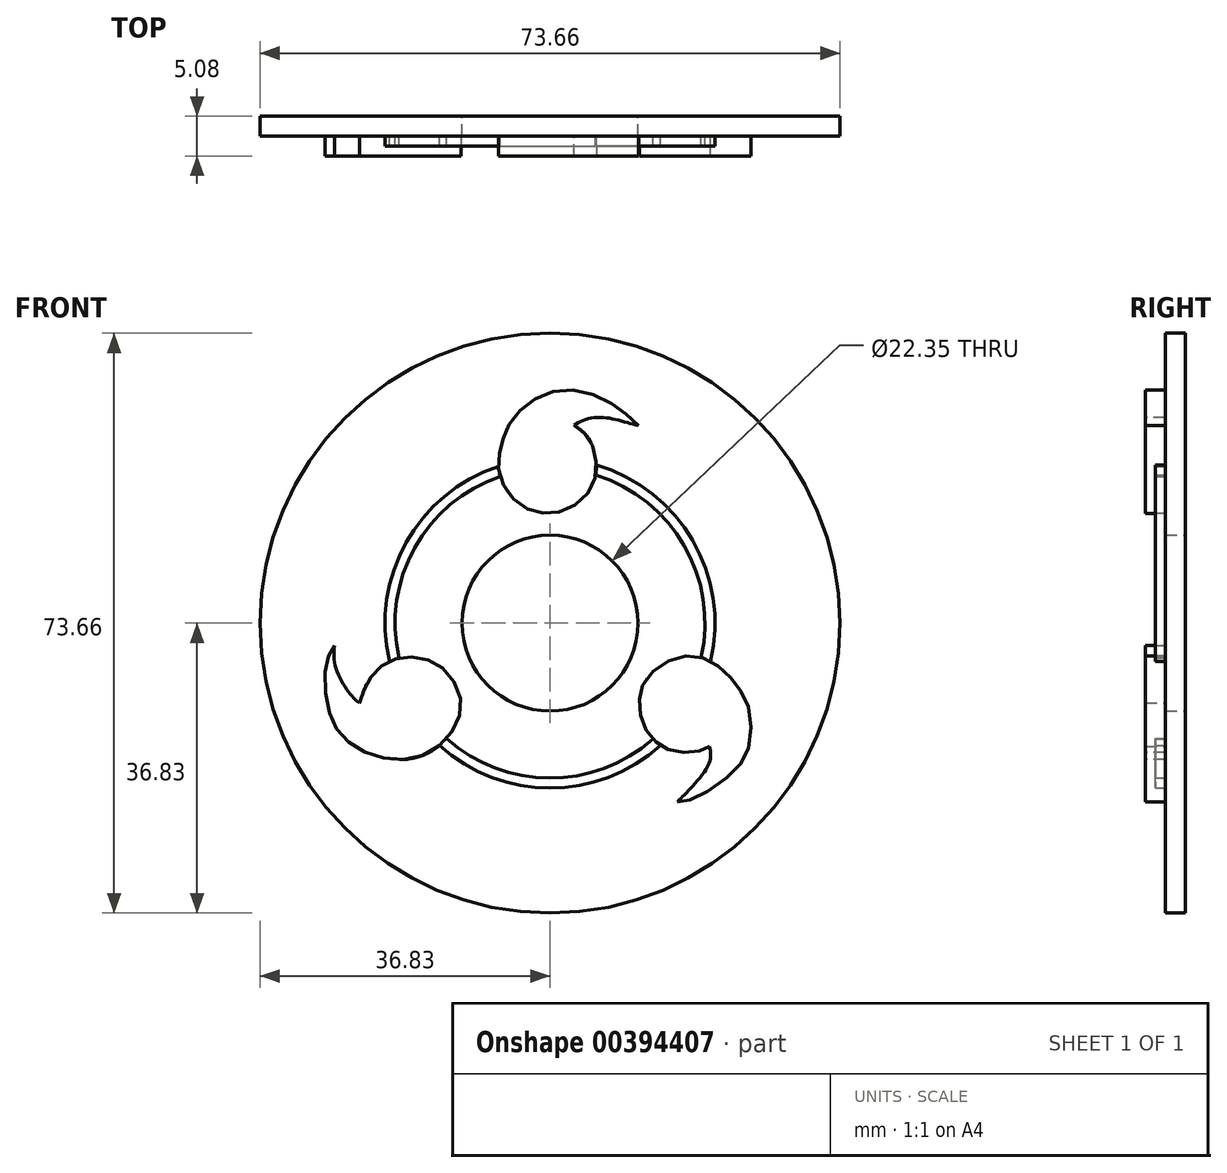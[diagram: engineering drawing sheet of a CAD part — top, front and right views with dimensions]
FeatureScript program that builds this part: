
annotation { "Feature Type Name" : "Feature", "Feature Type Description" : "" }
export const myFeature = defineFeature(function(context is Context, id is Id, definition is map)
    precondition{}
    {
        {
            var Q0;
            Q0=qCreatedBy(makeId("Front.planeOp"),FACE);
            var sketch = newSketch(context, id + "F0", { "sketchPlane" : qUnion([Q0])});
            skCircle(sketch, "E0", {"center": v(0, 0) * mm, "radius": 36.83 * mm});
            skSolve(sketch);
        }
        {
            var Q0;
            Q0=qCreatedBy(makeId("Front.planeOp"),FACE);
            var sketch = newSketch(context, id + "F1", { "sketchPlane" : qUnion([Q0])});
            skCircle(sketch, "E1", {"center": v(0, 0) * mm, "radius": 11.18 * mm});
            skSolve(sketch);
        }
        {
            var Q0;
            Q0=qCreatedBy(makeId("Front.planeOp"),FACE);
            var sketch = newSketch(context, id + "F2", { "sketchPlane" : qUnion([Q0])});
            skCircle(sketch, "E2", {"center": v(0, 0) * mm, "radius": 20.96 * mm});
            skCircle(sketch, "E3", {"center": v(0, 0) * mm, "radius": 19.69 * mm});
            skSolve(sketch);
        }
        {
            var Q0;
            Q0 = qSketchRegion(id + "F2", true);
            extrude(context, id + "F3", {"entities" : qUnion([Q0]), "depth" : 3.8 * mm});
        }
        {
            var Q0;
            Q0 = qSketchRegion(id + "F0", true);
            extrude(context, id + "F4", {"entities" : qUnion([Q0]), "operationType" : NewBodyOperationType.ADD, "depth" : 2.54 * mm});
        }
        {
            var Q0;
            Q0 = qSketchRegion(id + "F1", true);
            extrude(context, id + "F5", {"entities" : qUnion([Q0]), "operationType" : NewBodyOperationType.REMOVE, "depth" : 18.8 * mm, "offsetDistance" : 25.4 * mm});
        }
        {
            var Q0;
            Q0=qCreatedBy(makeId("Front.planeOp"),FACE);
            var sketch = newSketch(context, id + "F6", { "sketchPlane" : qUnion([Q0])});
            skFitSpline(sketch, "E4", {"points": [v(20.26, -15.67) * mm, v(19, -16.23) * mm, v(15.99, -16.33) * mm, v(13.64, -15.25) * mm, v(11.95, -13.04) * mm, v(11.34, -10.23) * mm, v(11.81, -7.79) * mm, v(14.53, -5.07) * mm, v(18.15, -4.18) * mm, v(21.29, -5.4) * mm, v(23.73, -7.88) * mm, v(25.28, -10.98) * mm, v(25.14, -16.05) * mm, v(22.98, -19.14) * mm, v(18.29, -22.29) * mm, v(16.18, -22.7) * mm], "startDerivative": vector(-24.78, -14.45) * mm, "endDerivative": vector(-34.66, -2.02) * mm});
            skFitSpline(sketch, "E5", {"points": [v(20.26, -15.67) * mm, v(20.26, -17.69) * mm, v(17.96, -20.88) * mm, v(16.18, -22.7) * mm], "startDerivative": vector(1.33, -6.74) * mm, "endDerivative": vector(-5.12, -5.1) * mm});
            skFitSpline(sketch, "E6", {"points": [v(3.05, 25.14) * mm, v(4.88, 23.55) * mm, v(5.86, 20.36) * mm, v(5.11, 16.93) * mm, v(1.92, 14.35) * mm, v(-1.5, 14.07) * mm, v(-4.74, 15.85) * mm, v(-6.48, 19.28) * mm, v(-6.24, 22.42) * mm, v(-5.11, 25.33) * mm, v(-1.92, 28.47) * mm, v(3.05, 29.6) * mm, v(8.16, 27.68) * mm, v(11.26, 25.1) * mm], "startDerivative": vector(32.58, -21.63) * mm, "endDerivative": vector(35.17, -33.59) * mm});
            skFitSpline(sketch, "E7", {"points": [v(11.26, 25.1) * mm, v(9.15, 25.66) * mm, v(6.8, 26.13) * mm, v(4.55, 25.9) * mm, v(3.05, 25.14) * mm], "startDerivative": vector(-8.21, 2.2) * mm, "endDerivative": vector(-6.28, -3.82) * mm});
            skFitSpline(sketch, "E8", {"points": [v(-23.92, -10.35) * mm, v(-24.72, -9.71) * mm, v(-26.06, -8.06) * mm, v(-27.34, -5.12) * mm, v(-27.4, -2.83) * mm], "startDerivative": vector(-4.4, 3.18) * mm, "endDerivative": vector(0.68, 8.42) * mm});
            skFitSpline(sketch, "E9", {"points": [v(-27.4, -2.83) * mm, v(-28.4, -5.02) * mm, v(-28.2, -10.73) * mm, v(-26.16, -14.57) * mm, v(-21.62, -17.03) * mm, v(-16.07, -16.76) * mm, v(-12.23, -13.4) * mm, v(-11.42, -9.4) * mm, v(-13.77, -5.6) * mm, v(-17.35, -4.32) * mm, v(-20.88, -5.07) * mm, v(-23.17, -7.52) * mm, v(-24.18, -10.17) * mm], "startDerivative": vector(-18.88, -28.65) * mm, "endDerivative": vector(-11.45, -38.62) * mm});
            skSolve(sketch);
        }
        {
            var Q0;
            Q0 = qSketchRegion(id + "F6", true);
            extrude(context, id + "F7", {"entities" : qUnion([Q0]), "operationType" : NewBodyOperationType.ADD, "depth" : 5.08 * mm});
        }
    });
